# Revit family: 3097105 Lighting Fixture_Sylvania_Insaver LED 75 Square White Bezel_Ceiling Recessed
name_source: partatom
category: Lighting Fixtures
revit_build: Autodesk Revit 2017 (Build: 20190507_1515(x64)
units: mm (PartAtom-declared; Revit-internal decimal feet)

## family parameters
Cut with Voids When Loaded = No
Host = Face
Light Source = Yes
OmniClass Number = 23.80.70.11.17
OmniClass Title = Specialized Lighting by Location or Use
Part Type = Normal
Room Calculation Point = No
Round Connector Dimension = Use Diameter
Shared = No

## types (2) — shared parameters
Apparent Load = 16 VA
Assembly Code = D5020200
Beam Angle = Wide
Body Material = Aluminum_Sylvania_Insaver 75 LED_White
CRI ( Ra ) = 80
Color Filter = 16777215
Cutout Length = 75 mm  [stored 0.246063 ft]
Cutout Width = 75 mm  [stored 0.246063 ft]
Description = 16W to 38W LED white downlight. Harnesing the power of Mid Power LEDs. Ideal for applications such as reception areas, offices, general public circulation areas, corridors or and any location that requires long service hours and high switching cycles. Choice of 3,000K warm white or 4,000K neutral white colour temperature. IP44 with accessory. IP65 as standard on Insaver 75. High lumen output - up to 2,922lm. Cost effective product - will help you comply with Building regulations - up to 73lm/W. Available in Low profile as well as well as Low glare versions. Available in DALI versions. Available in Emergency versions. Quick and easy to install. LED technology provides energy efficient solution and reduced maintenance costs and long lifetime. To discover for yourself how much your business can save on its energy bills, simply visit our online Savings Calculator at: www.havells-sylvania.com
Diffuser Material = Polycarbonate_Sylvania_Insaver 75 LED_Clear
Dimming Lamp Color Temperature Shift = <None>
Drive Current = 350mA
Electrical Protection = CLASS II
Emit Shape Visible in Rendering = No
Emit from Rectangle Length = 67 mm  [stored 0.219816 ft]
Emit from Rectangle Width = 67 mm  [stored 0.219816 ft]
Height = 65 mm  [stored 0.213255 ft]
IK Rating = IK02
IP Rating = IP65
Lamp = Integrated LED
Length = 90 mm  [stored 0.295276 ft]
Life = 50 000h
Manufacturer = Feilo Sylvania
Product Family = Insaver 75 LED Square White Bezel
Product Page URL = http://www.sylvania-lighting.com
Reflector Material = Metal_Sylvania_Insaver 75 LED_Silver
Tilt Angle = -90.00°
URL = http://www.sylvania-lighting.com
Voltage = 240 V
Voltage Comments = UNV (Universal Voltage; 220-240 Volt)
Weight = 0.40 kg
Width = 90 mm  [stored 0.295276 ft]
zero-valued in all types: Default Elevation

## per-type parameters (varying)
| type | Model | Photometric Web File |
| Insaver 75 LED SQ WW DB WH | 3097104 Insaver 75 LED SQ WW DB WH | 3097104_Insaver75LEDSQWWDBWH-185552.ies |
| Insaver 75 LED SQ 16W NW DB WH | 3097105 Insaver 75 LED SQ 16W NW DB WH | 3097105_Insaver75LEDSQNWDBWH-185565.ies |

note: [stored X ft] marks values corroborated as IEEE doubles in the binary element streams (Revit-internal decimal feet)

## geometry (parser evidence)
native form markers: Blend x8, Sweep x1
no freeform markers — native parametric forms only
